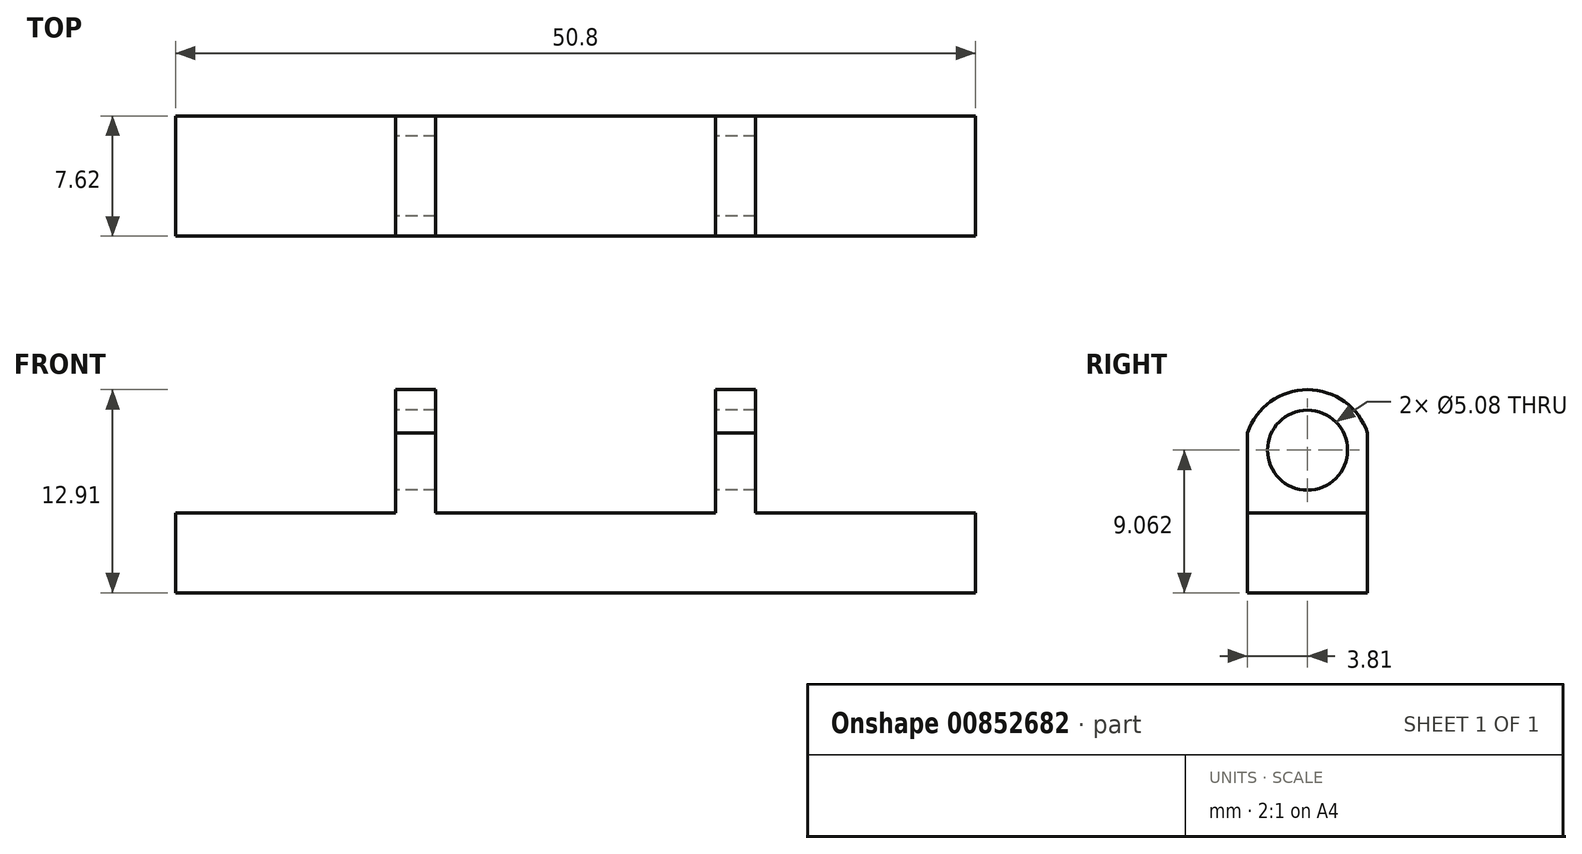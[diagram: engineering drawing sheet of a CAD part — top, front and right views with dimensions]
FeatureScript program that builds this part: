
annotation { "Feature Type Name" : "Feature", "Feature Type Description" : "" }
export const myFeature = defineFeature(function(context is Context, id is Id, definition is map)
    precondition{}
    {
        {
            var Q0;
            Q0=qCreatedBy(makeId("Front.planeOp"),FACE);
            var sketch = newSketch(context, id + "F0", { "sketchPlane" : qUnion([Q0])});
            skLineSegment(sketch, "E0", {"start": v(0, 0) * mm, "end": v(25.4, 0) * mm});
            skLineSegment(sketch, "E1", {"start": v(0, 0) * mm, "end": v(-25.4, 0) * mm});
            skLineSegment(sketch, "E2", {"start": v(-25.4, 0) * mm, "end": v(-25.4, -5.08) * mm});
            skLineSegment(sketch, "E3", {"start": v(-25.4, -5.08) * mm, "end": v(25.4, -5.08) * mm});
            skLineSegment(sketch, "E4", {"start": v(25.4, 0) * mm, "end": v(25.4, -5.08) * mm});
            skLineSegment(sketch, "E5", {"start": v(0, 0) * mm, "end": v(8.9, 0) * mm});
            skLineSegment(sketch, "E6", {"start": v(8.9, 0) * mm, "end": v(8.9, 5.08) * mm});
            skLineSegment(sketch, "E7", {"start": v(8.9, 5.08) * mm, "end": v(11.43, 5.08) * mm});
            skLineSegment(sketch, "E8", {"start": v(11.43, 5.08) * mm, "end": v(11.43, 0) * mm});
            skLineSegment(sketch, "E9.MirrorCS", {"start": v(-8.9, 0) * mm, "end": v(-8.9, 5.08) * mm});
            skLineSegment(sketch, "E10.MirrorCS", {"start": v(-11.43, 5.08) * mm, "end": v(-11.43, 0) * mm});
            skLineSegment(sketch, "E11.MirrorCS", {"start": v(-8.9, 5.08) * mm, "end": v(-11.43, 5.08) * mm});
            skSolve(sketch);
        }
        {
            var Q0;
            Q0=makeQuery(id+"F0.imprint","IMPRINT",FACE,{"disambiguationData":[TD([[makeQuery(id+"F0.imprint","IMPRINT",EDGE,{"derivedFrom":sQuery(id+"F0.wireOp",EDGE,"E0")}),-1.0]])]});
            extrude(context, id + "F1", {"entities" : qUnion([Q0]), "depth" : 7.62 * mm, "offsetDistance" : 25.4 * mm});
        }
        {
            var Q0;
            Q0=makeQuery(id+"F0.imprint","IMPRINT",FACE,{"disambiguationData":[TD([[makeQuery(id+"F0.imprint","IMPRINT",EDGE,{"derivedFrom":sQuery(id+"F0.wireOp",EDGE,"E0")}),-1.0]])]});
            extrude(context, id + "F2", {"entities" : qUnion([Q0]), "operationType" : NewBodyOperationType.ADD, "depth" : 7.62 * mm, "offsetDistance" : 25.4 * mm});
        }
        {
            var Q0;
            {var subQ0=sQuery(id+"F0.wireOp",EDGE,"E9.MirrorCS");Q0=makeQuery(id+"F0.imprint","IMPRINT",FACE,{"disambiguationData":[TD([[makeQuery(id+"F0.imprint","IMPRINT",EDGE,{"derivedFrom":subQ0}),1.0]])]});}
            var Q1;
            {var subQ0=sQuery(id+"F0.wireOp",EDGE,"E6");Q1=makeQuery(id+"F0.imprint","IMPRINT",FACE,{"disambiguationData":[TD([[makeQuery(id+"F0.imprint","IMPRINT",EDGE,{"derivedFrom":subQ0}),-1.0]])]});}
            var Q2;
            Q2 = qSketchRegion(id + "F4", true);
            extrude(context, id + "F3", {"entities" : qUnion([Q0, Q1, Q2]), "operationType" : NewBodyOperationType.ADD, "depth" : 7.62 * mm, "offsetDistance" : 25.4 * mm});
        }
        {
            var Q0;
            Q0=makeQuery(id+"F3.opExtrude","SWEPT_FACE",FACE,{"disambiguationData":[OSD([sQuery(id+"F0.wireOp",EDGE,"E10.MirrorCS")])]});
            var sketch = newSketch(context, id + "F4", { "sketchPlane" : qUnion([Q0])});
            skArc(sketch, "E12", {"start": v(7.62, 5.08) * mm, "mid": v(3.81, 7.83) * mm, "end": v(0, 5.08) * mm});
            skPoint(sketch, "E12.first.point", {"position": v(0, 5.08) * mm});
            skPoint(sketch, "E12.third.point", {"position": v(7.62, 5.08) * mm});
            skPoint(sketch, "E13.end.orphan", {"position": v(2.54, 7.62) * mm});
            skPoint(sketch, "E13.start.orphan", {"position": v(3.81, 5.08) * mm});
            skCircle(sketch, "E14", {"center": v(3.81, 3.98) * mm, "radius": 2.54 * mm});
            skSolve(sketch);
        }
        {
            var Q0;
            {var subQ0=sQuery(id+"F4.wireOp",EDGE,"E12");Q0=makeQuery(id+"F4.imprint","IMPRINT",FACE,{"disambiguationData":[TD([[makeQuery(id+"F4.imprint","IMPRINT",EDGE,{"derivedFrom":subQ0}),1.0]])]});}
            extrude(context, id + "F5", {"entities" : qUnion([Q0]), "operationType" : NewBodyOperationType.ADD, "depth" : -2.54 * mm, "offsetDistance" : 25.4 * mm});
        }
        {
            var Q0;
            {var subQ0=sQuery(id+"F4.wireOp",EDGE,"E14");var subQ1=makeQuery(id+"F3.opExtrude","SWEPT_EDGE",EDGE,{"disambiguationData":[OSD([sQuery(id+"F0.wireOp",EDGE,"E10.MirrorCS"),sQuery(id+"F0.wireOp",EDGE,"E11.MirrorCS")])]});var subQ2=makeQuery(id+"F4.imprint","INTERSECT",VERTEX,{"disambiguationData":[OD(0.0)],"derivedFrom":[subQ1,subQ0]});Q0=makeQuery(id+"F4.imprint","IMPRINT",FACE,{"disambiguationData":[TD([[makeQuery(id+"F4.imprint","IMPRINT",EDGE,{"disambiguationData":[TD([[subQ2,-1.0]])],"derivedFrom":subQ0}),1.0]])]});}
            extrude(context, id + "F6", {"entities" : qUnion([Q0]), "operationType" : NewBodyOperationType.REMOVE, "endBound" : BoundingType.THROUGH_ALL, "oppositeDirection" : true, "depth" : 25.4 * mm, "offsetDistance" : 25.4 * mm});
        }
        {
            var Q0;
            Q0=makeQuery(id+"F1.opExtrude","SWEPT_BODY",BODY,{"disambiguationData":[OSD([sQuery(id+"F0.wireOp",EDGE,"E0"),sQuery(id+"F0.wireOp",EDGE,"E1"),sQuery(id+"F0.wireOp",EDGE,"E2"),sQuery(id+"F0.wireOp",EDGE,"E3"),sQuery(id+"F0.wireOp",EDGE,"E4"),sQuery(id+"F0.wireOp",EDGE,"E5")])]});
            var Q1;
            Q1=qCreatedBy(makeId("Right.planeOp"),FACE);
            mirror(context, id + "F7", {"operationType" : NewBodyOperationType.ADD, "entities" : qUnion([Q0]), "mirrorPlane" : qUnion([Q1])});
        }
    });
